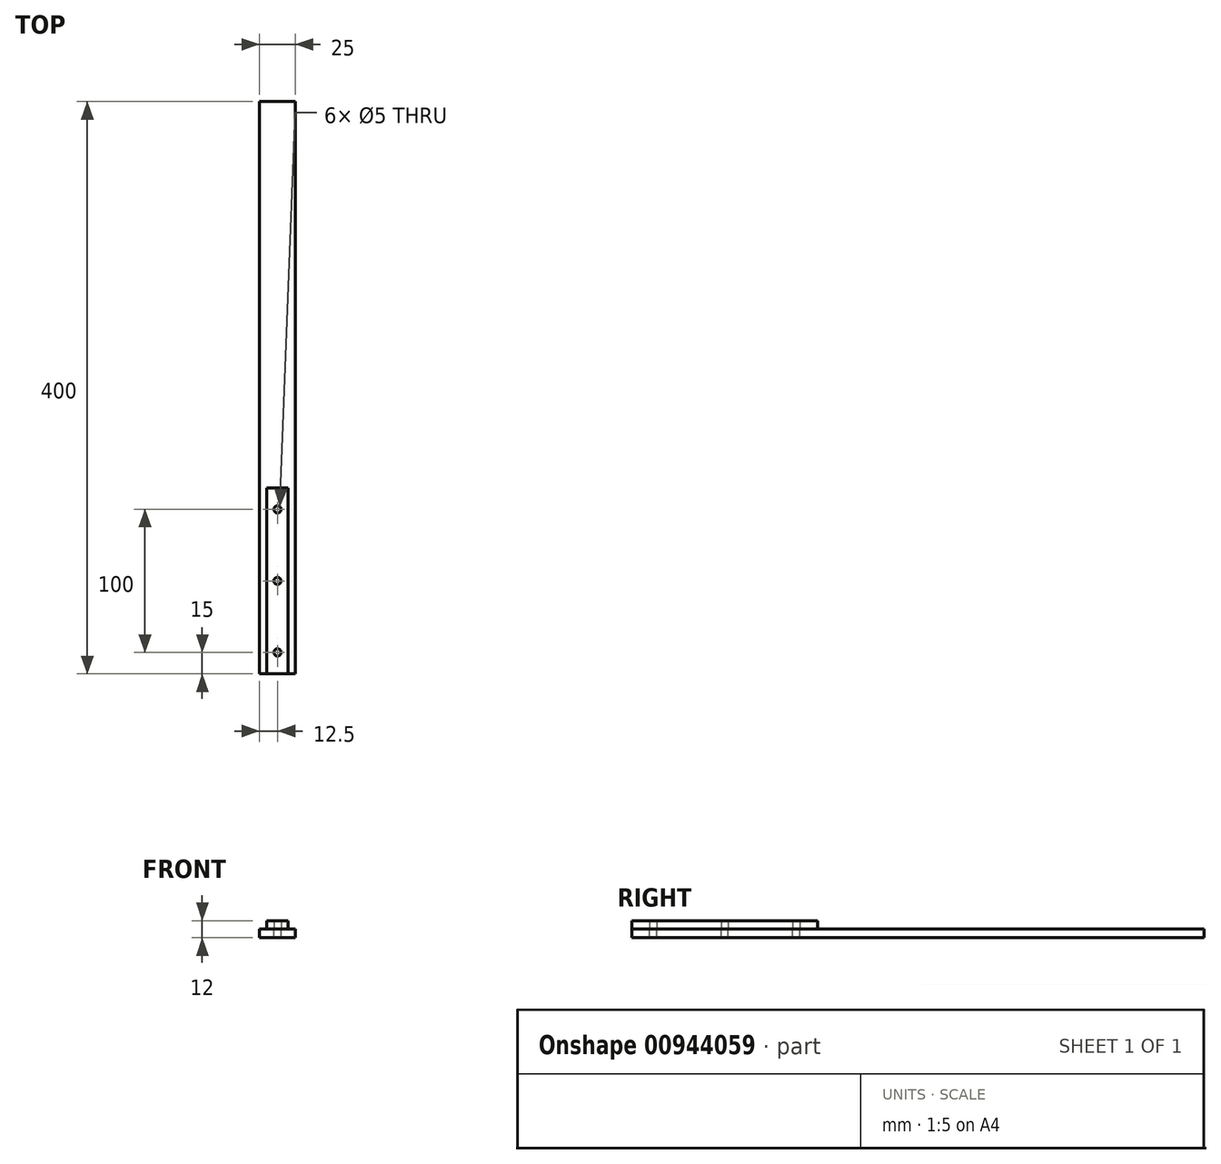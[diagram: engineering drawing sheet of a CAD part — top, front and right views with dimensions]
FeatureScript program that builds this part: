
annotation { "Feature Type Name" : "Feature", "Feature Type Description" : "" }
export const myFeature = defineFeature(function(context is Context, id is Id, definition is map)
    precondition{}
    {
        {
            var Q0;
            Q0=qCreatedBy(makeId("Top.planeOp"),FACE);
            var sketch = newSketch(context, id + "F0", { "sketchPlane" : qUnion([Q0])});
            skLineSegment(sketch, "E0.bottom", {"start": v(-12.5, -200) * mm, "end": v(12.5, -200) * mm});
            skLineSegment(sketch, "E0.top", {"start": v(-12.5, 200) * mm, "end": v(12.5, 200) * mm});
            skLineSegment(sketch, "E0.left", {"start": v(-12.5, -200) * mm, "end": v(-12.5, 200) * mm});
            skLineSegment(sketch, "E0.right", {"start": v(12.5, -200) * mm, "end": v(12.5, 200) * mm});
            skPoint(sketch, "E0.middle", {"position": v(0, 0) * mm});
            skLineSegment(sketch, "E1", {"start": v(0, -200) * mm, "end": v(0, 200) * mm, "construction": true});
            skPoint(sketch, "E2", {"position": v(0, -185) * mm});
            skPoint(sketch, "E3", {"position": v(0, -135) * mm});
            skPoint(sketch, "E4", {"position": v(0, -85) * mm});
            skLineSegment(sketch, "E5", {"start": v(-7.5, -70) * mm, "end": v(7.5, -70) * mm});
            skLineSegment(sketch, "E6.0", {"start": v(-7.5, -200) * mm, "end": v(-7.5, -70) * mm});
            skLineSegment(sketch, "E7.0", {"start": v(7.5, -200) * mm, "end": v(7.5, -70) * mm});
            skSolve(sketch);
        }
        {
            var Q0;
            Q0=makeQuery(id+"F0.imprint","IMPRINT",FACE,{"disambiguationData":[TD([[makeQuery(id+"F0.imprint","IMPRINT",EDGE,{"derivedFrom":sQuery(id+"F0.wireOp",EDGE,"E0.top")}),-1.0]])]});
            var Q1;
            Q1=makeQuery(id+"F0.imprint","IMPRINT",FACE,{"disambiguationData":[TD([[makeQuery(id+"F0.imprint","IMPRINT",EDGE,{"derivedFrom":sQuery(id+"F0.wireOp",EDGE,"E5")}),-1.0]])]});
            extrude(context, id + "F1", {"entities" : qUnion([Q0, Q1]), "depth" : -6 * mm, "offsetDistance" : 25 * mm});
        }
        {
            var Q0;
            Q0=makeQuery(id+"F0.imprint","IMPRINT",FACE,{"disambiguationData":[TD([[makeQuery(id+"F0.imprint","IMPRINT",EDGE,{"derivedFrom":sQuery(id+"F0.wireOp",EDGE,"E5")}),-1.0]])]});
            extrude(context, id + "F2", {"entities" : qUnion([Q0]), "depth" : 6 * mm, "offsetDistance" : 25 * mm});
        }
        {
            var Q0;
            Q0=sQuery(id+"F0.wireOp",VERTEX,"E3");
            var Q1;
            Q1=sQuery(id+"F0.wireOp",VERTEX,"E2");
            var Q2;
            Q2=sQuery(id+"F0.wireOp",VERTEX,"E4");
            var Q3;
            Q3=makeQuery(id+"F1.opExtrude","SWEPT_BODY",BODY,{"disambiguationData":[OSD([sQuery(id+"F0.wireOp",EDGE,"E0.bottom"),sQuery(id+"F0.wireOp",EDGE,"E0.top"),sQuery(id+"F0.wireOp",EDGE,"E0.left"),sQuery(id+"F0.wireOp",EDGE,"E0.right")])]});
            hole(context, id + "F3", {"style" : HoleStyle.SIMPLE, "endStyle" : HoleEndStyle.THROUGH, "holeDiameter" : 5 * mm, "majorDiameter" : 5 * mm, "isTappedThrough" : true, "tappedDepth" : 12 * mm, "tapClearance" : 3, "locations" : qUnion([Q0, Q1, Q2]), "scope" : qUnion([Q3])});
        }
        {
            var Q0;
            Q0=sQuery(id+"F0.wireOp",VERTEX,"E2");
            var Q1;
            Q1=sQuery(id+"F0.wireOp",VERTEX,"E3");
            var Q2;
            Q2=sQuery(id+"F0.wireOp",VERTEX,"E4");
            var Q3;
            Q3=makeQuery(id+"F2.opExtrude","SWEPT_BODY",BODY,{"disambiguationData":[OSD([sQuery(id+"F0.wireOp",EDGE,"E0.bottom"),sQuery(id+"F0.wireOp",EDGE,"E5"),sQuery(id+"F0.wireOp",EDGE,"E6.0"),sQuery(id+"F0.wireOp",EDGE,"E7.0")])]});
            hole(context, id + "F4", {"style" : HoleStyle.SIMPLE, "endStyle" : HoleEndStyle.THROUGH, "oppositeDirection" : true, "holeDiameter" : 5 * mm, "majorDiameter" : 5 * mm, "isTappedThrough" : true, "tappedDepth" : 12 * mm, "tapClearance" : 3, "locations" : qUnion([Q0, Q1, Q2]), "scope" : qUnion([Q3])});
        }
    });
